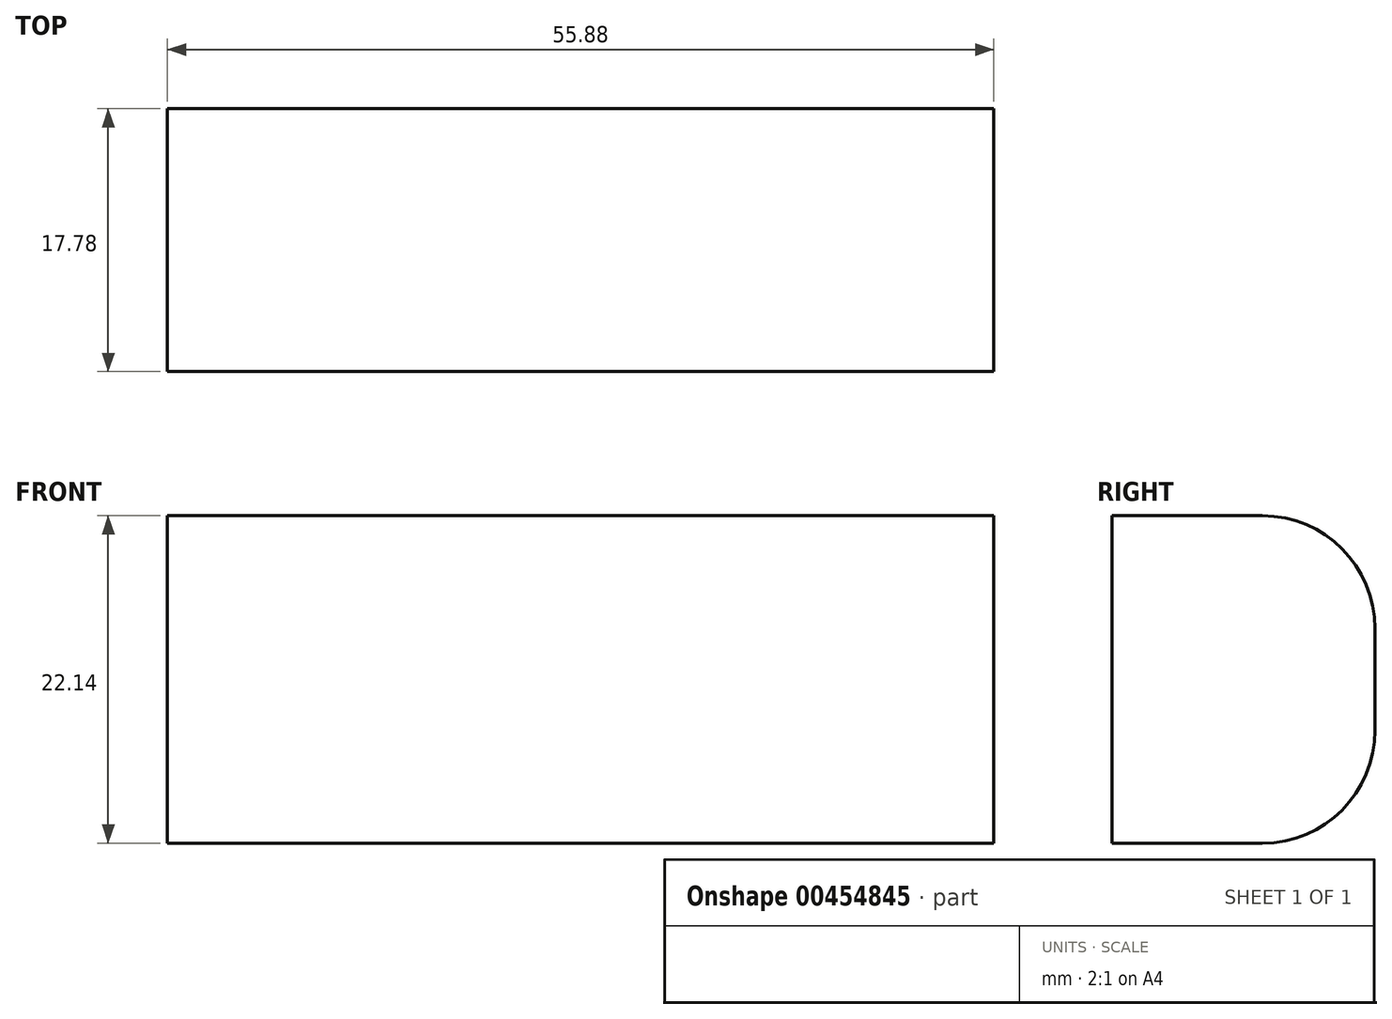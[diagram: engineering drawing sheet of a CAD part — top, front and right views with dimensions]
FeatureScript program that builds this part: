
annotation { "Feature Type Name" : "Feature", "Feature Type Description" : "" }
export const myFeature = defineFeature(function(context is Context, id is Id, definition is map)
    precondition{}
    {
        {
            var Q0;
            Q0=qCreatedBy(makeId("Front.planeOp"),FACE);
            var sketch = newSketch(context, id + "F0", { "sketchPlane" : qUnion([Q0])});
            skLineSegment(sketch, "E0.bottom", {"start": v(27.94, -11.07) * mm, "end": v(-27.94, -11.07) * mm});
            skLineSegment(sketch, "E0.top", {"start": v(27.94, 11.07) * mm, "end": v(-27.94, 11.07) * mm});
            skLineSegment(sketch, "E0.left", {"start": v(27.94, -11.07) * mm, "end": v(27.94, 11.07) * mm});
            skLineSegment(sketch, "E0.right", {"start": v(-27.94, -11.07) * mm, "end": v(-27.94, 11.07) * mm});
            skPoint(sketch, "E0.middle", {"position": v(0, 0) * mm});
            skSolve(sketch);
        }
        {
            var Q0;
            Q0 = qSketchRegion(id + "F0", true);
            extrude(context, id + "F1", {"entities" : qUnion([Q0]), "endBound" : BoundingType.SYMMETRIC, "depth" : 17.78 * mm, "offsetDistance" : 25.4 * mm});
        }
        {
            var Q0;
            Q0=makeQuery(id+"F1.opExtrude","CAP_EDGE",EDGE,{"disambiguationData":[OSD([sQuery(id+"F0.wireOp",EDGE,"E0.top")])],"isStart":true});
            var Q1;
            Q1=makeQuery(id+"F1.opExtrude","CAP_EDGE",EDGE,{"disambiguationData":[OSD([sQuery(id+"F0.wireOp",EDGE,"E0.bottom")])],"isStart":true});
            fillet(context, id + "F2", {"entities" : qUnion([Q0, Q1]), "radius" : 7.62 * mm, "tangentPropagation" : true, "allowEdgeOverflow" : false});
        }
    });
